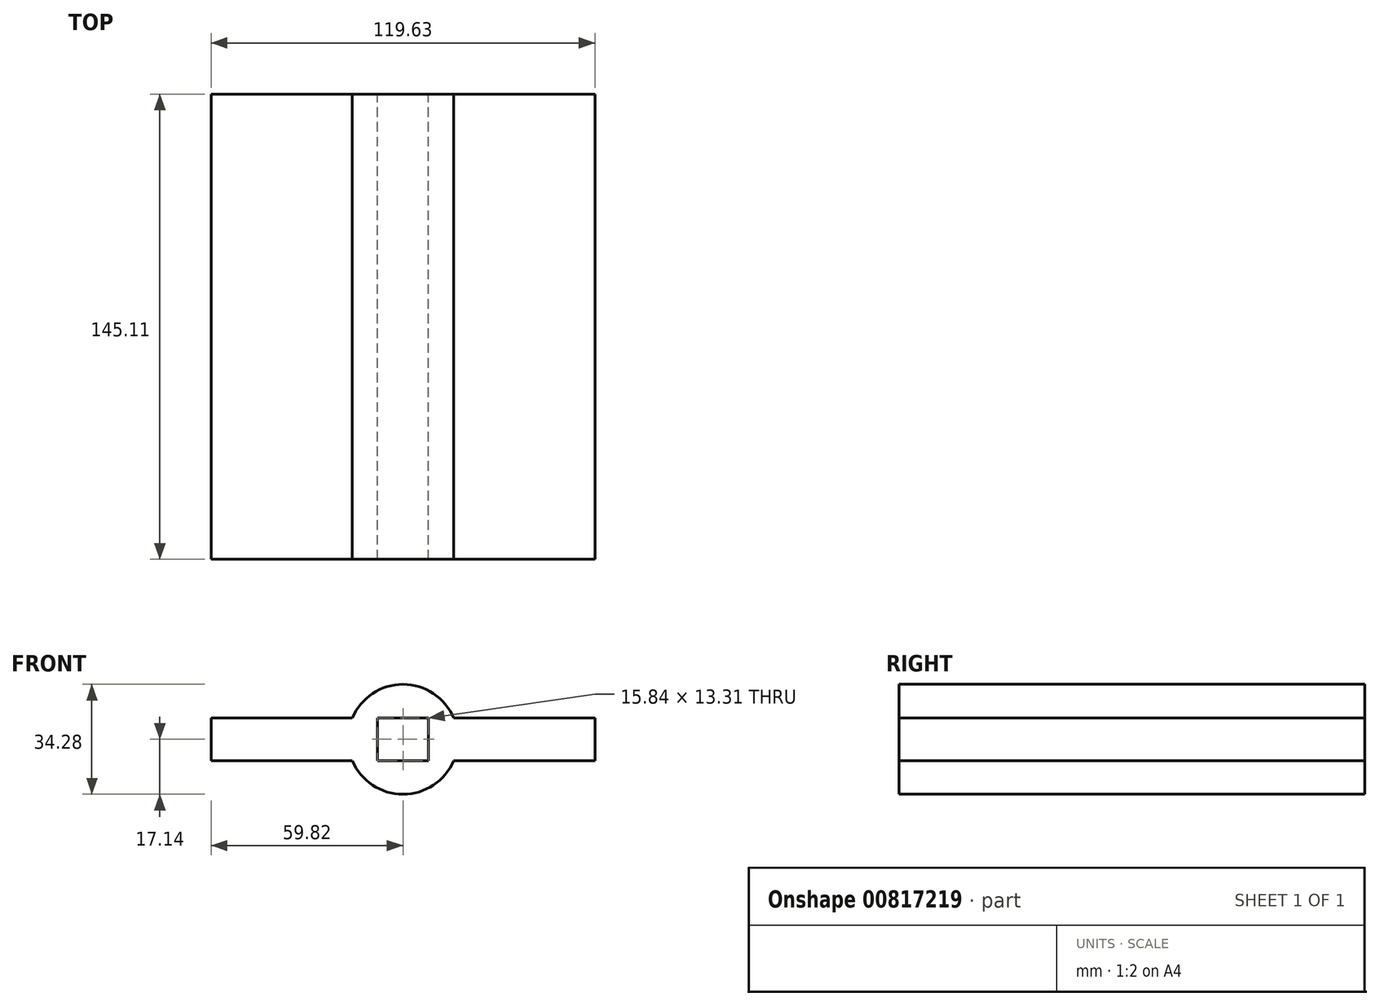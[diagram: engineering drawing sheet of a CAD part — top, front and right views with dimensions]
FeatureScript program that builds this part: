
annotation { "Feature Type Name" : "Feature", "Feature Type Description" : "" }
export const myFeature = defineFeature(function(context is Context, id is Id, definition is map)
    precondition{}
    {
        {
            var Q0;
            Q0=qCreatedBy(makeId("Front.planeOp"),FACE);
            var sketch = newSketch(context, id + "F0", { "sketchPlane" : qUnion([Q0])});
            skCircle(sketch, "E0", {"center": v(0, 0) * mm, "radius": 17.14 * mm});
            skSolve(sketch);
        }
        {
            var Q0;
            Q0=makeQuery(id+"F0.imprint","IMPRINT",FACE,{"disambiguationData":[TD([[makeQuery(id+"F0.imprint","IMPRINT",EDGE,{"derivedFrom":sQuery(id+"F0.wireOp",EDGE,"E0")}),1.0]])]});
            extrude(context, id + "F1", {"entities" : qUnion([Q0]), "depth" : 145.11 * mm, "offsetDistance" : 25.4 * mm});
        }
        {
            var Q0;
            Q0=qCreatedBy(makeId("Front.planeOp"),FACE);
            var sketch = newSketch(context, id + "F2", { "sketchPlane" : qUnion([Q0])});
            skLineSegment(sketch, "E1.bottom", {"start": v(-7.92, -6.65) * mm, "end": v(7.92, -6.65) * mm});
            skLineSegment(sketch, "E1.top", {"start": v(-7.92, 6.65) * mm, "end": v(7.92, 6.65) * mm});
            skLineSegment(sketch, "E1.left", {"start": v(-7.92, -6.65) * mm, "end": v(-7.92, 6.65) * mm});
            skLineSegment(sketch, "E1.right", {"start": v(7.92, -6.65) * mm, "end": v(7.92, 6.65) * mm});
            skPoint(sketch, "E1.middle", {"position": v(0, 0) * mm});
            skSolve(sketch);
        }
        {
            var Q0;
            Q0=makeQuery(id+"F2.imprint","IMPRINT",FACE,{"disambiguationData":[TD([[makeQuery(id+"F2.imprint","IMPRINT",EDGE,{"derivedFrom":sQuery(id+"F2.wireOp",EDGE,"E1.bottom")}),1.0]])]});
            var Q1;
            Q1=sQuery(id+"F2.wireOp",EDGE,"E1.top");
            var Q2;
            Q2=sQuery(id+"F2.wireOp",EDGE,"E1.left");
            var Q3;
            Q3=sQuery(id+"F2.wireOp",EDGE,"E1.bottom");
            var Q4;
            Q4=sQuery(id+"F2.wireOp",EDGE,"E1.right");
            extrude(context, id + "F3", {"entities" : qUnion([Q0]), "operationType" : NewBodyOperationType.REMOVE, "surfaceEntities" : qUnion([Q1, Q2, Q3, Q4]), "depth" : 239.87 * mm, "offsetDistance" : 25.4 * mm});
        }
        {
            var Q0;
            Q0=makeQuery(id+"F3.boolean.opBoolean","COPY",FACE,{"derivedFrom":makeQuery(id+"F3.opExtrude","SWEPT_FACE",FACE,{"disambiguationData":[OSD([sQuery(id+"F2.wireOp",EDGE,"E1.left")])]})});
            extrude(context, id + "F4", {"entities" : qUnion([Q0]), "operationType" : NewBodyOperationType.ADD, "oppositeDirection" : true, "depth" : 51.9 * mm, "offsetDistance" : 25.4 * mm});
        }
        {
            var Q0;
            Q0=makeQuery(id+"F3.boolean.opBoolean","COPY",FACE,{"derivedFrom":makeQuery(id+"F3.opExtrude","SWEPT_FACE",FACE,{"disambiguationData":[OSD([sQuery(id+"F2.wireOp",EDGE,"E1.right")])]})});
            extrude(context, id + "F5", {"entities" : qUnion([Q0]), "operationType" : NewBodyOperationType.ADD, "oppositeDirection" : true, "depth" : 51.9 * mm, "offsetDistance" : 25.4 * mm});
        }
    });
